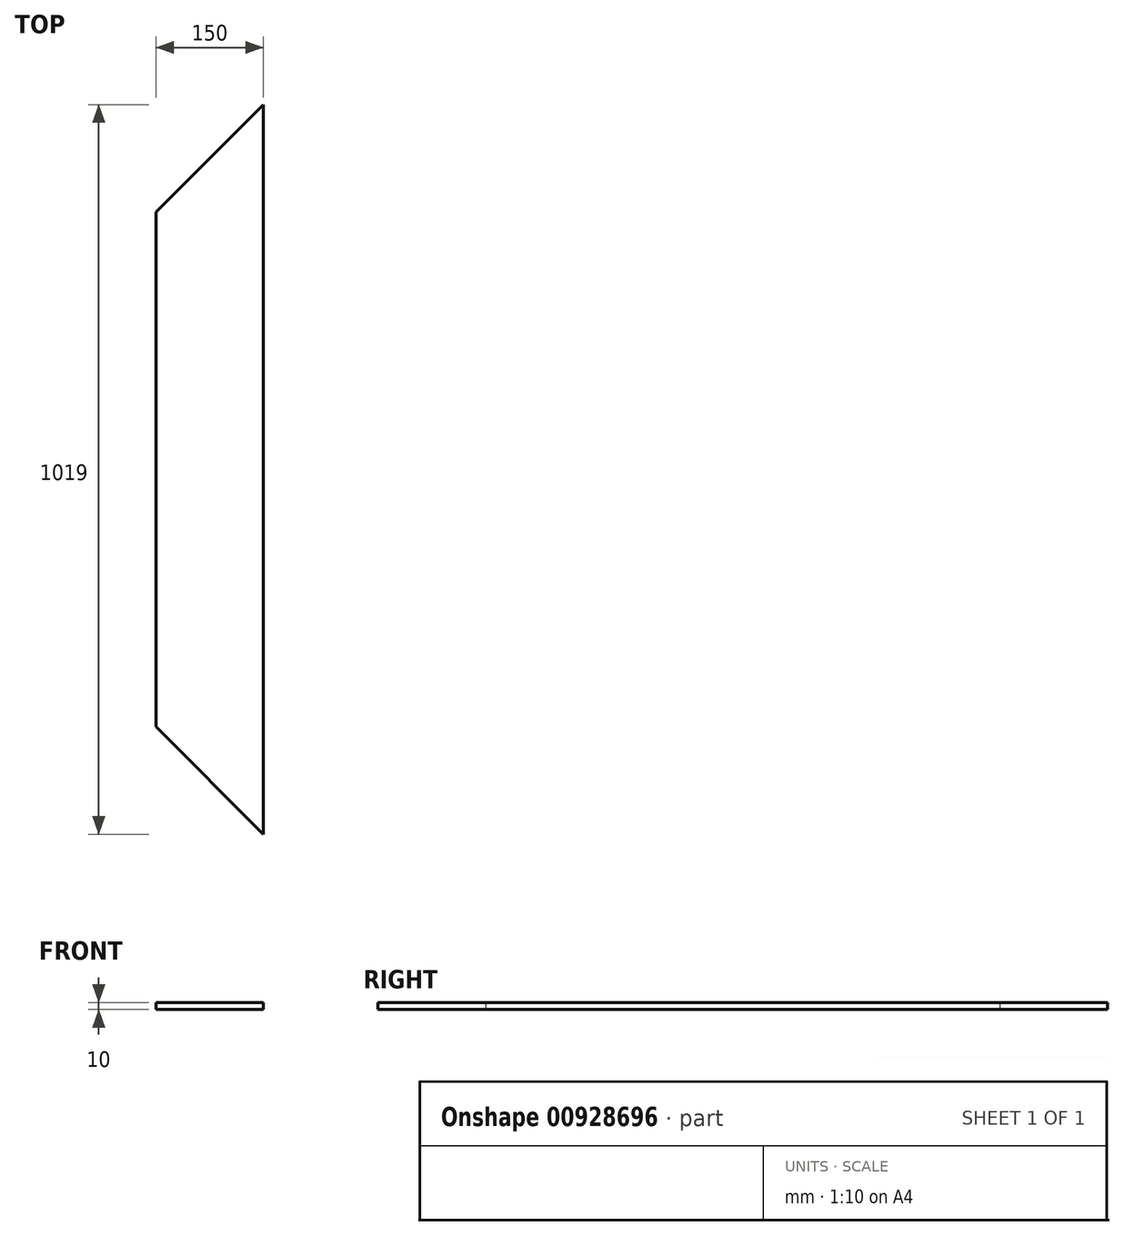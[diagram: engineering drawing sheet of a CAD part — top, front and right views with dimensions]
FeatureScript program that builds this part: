
annotation { "Feature Type Name" : "Feature", "Feature Type Description" : "" }
export const myFeature = defineFeature(function(context is Context, id is Id, definition is map)
    precondition{}
    {
        {
            var Q0;
            Q0=qCreatedBy(makeId("Front.planeOp"),FACE);
            var sketch = newSketch(context, id + "F0", { "sketchPlane" : qUnion([Q0])});
            skLineSegment(sketch, "E0.bottom", {"start": v(-74.52, -26.74) * mm, "end": v(75.48, -26.74) * mm});
            skLineSegment(sketch, "E0.top", {"start": v(-74.52, -36.74) * mm, "end": v(75.48, -36.74) * mm});
            skLineSegment(sketch, "E0.left", {"start": v(-74.52, -26.74) * mm, "end": v(-74.52, -36.74) * mm});
            skLineSegment(sketch, "E0.right", {"start": v(75.48, -26.74) * mm, "end": v(75.48, -36.74) * mm});
            skSolve(sketch);
        }
        {
            var Q0;
            Q0 = qSketchRegion(id + "F0", true);
            extrude(context, id + "F1", {"entities" : qUnion([Q0]), "depth" : 1019 * mm, "offsetDistance" : 25 * mm});
        }
        {
            var Q0;
            Q0=makeQuery(id+"F1.opExtrude","SWEPT_FACE",FACE,{"disambiguationData":[OSD([sQuery(id+"F0.wireOp",EDGE,"E0.bottom")])]});
            var sketch = newSketch(context, id + "F2", { "sketchPlane" : qUnion([Q0])});
            skLineSegment(sketch, "E1", {"start": v(75.48, 0) * mm, "end": v(-74.52, -150) * mm});
            skLineSegment(sketch, "E2", {"start": v(-74.52, -150) * mm, "end": v(-107.99, -156.75) * mm});
            skLineSegment(sketch, "E3", {"start": v(-164.14, -150) * mm, "end": v(-164.14, 159.84) * mm});
            skLineSegment(sketch, "E4", {"start": v(-164.14, 159.84) * mm, "end": v(178, 169.1) * mm});
            skLineSegment(sketch, "E5", {"start": v(178, 169.1) * mm, "end": v(75.48, 0) * mm});
            skLineSegment(sketch, "E6", {"start": v(-107.99, -156.75) * mm, "end": v(-164.14, -150) * mm});
            skSolve(sketch);
        }
        {
            var Q0;
            Q0 = qSketchRegion(id + "F2", true);
            var Q1;
            Q1=sQuery(id+"F2.wireOp",EDGE,"E1");
            extrude(context, id + "F3", {"entities" : qUnion([Q0]), "operationType" : NewBodyOperationType.REMOVE, "surfaceEntities" : qUnion([Q1]), "endBound" : BoundingType.THROUGH_ALL, "oppositeDirection" : true, "depth" : 25 * mm, "offsetDistance" : 25 * mm, "hasSecondDirection" : true, "secondDirectionBound" : SecondDirectionBoundingType.THROUGH_ALL, "secondDirectionOppositeDirection" : false, "secondDirectionDepth" : 25 * mm});
        }
        {
            var Q0;
            Q0=makeQuery(id+"F1.opExtrude","SWEPT_FACE",FACE,{"disambiguationData":[OSD([sQuery(id+"F0.wireOp",EDGE,"E0.bottom")])]});
            var sketch = newSketch(context, id + "F4", { "sketchPlane" : qUnion([Q0])});
            skLineSegment(sketch, "E7", {"start": v(75.48, -1019) * mm, "end": v(-74.52, -869) * mm});
            skLineSegment(sketch, "E8", {"start": v(-74.52, -869) * mm, "end": v(-237.24, -869) * mm});
            skLineSegment(sketch, "E9", {"start": v(-237.24, -869) * mm, "end": v(-237.24, -1200.16) * mm});
            skLineSegment(sketch, "E10", {"start": v(-237.24, -1200.16) * mm, "end": v(72.76, -1200.16) * mm});
            skLineSegment(sketch, "E11", {"start": v(72.76, -1200.16) * mm, "end": v(75.48, -1019) * mm});
            skSolve(sketch);
        }
        {
            var Q0;
            Q0 = qSketchRegion(id + "F4", true);
            extrude(context, id + "F5", {"entities" : qUnion([Q0]), "operationType" : NewBodyOperationType.REMOVE, "endBound" : BoundingType.THROUGH_ALL, "depth" : 25 * mm, "offsetDistance" : 25 * mm, "hasSecondDirection" : true, "secondDirectionBound" : SecondDirectionBoundingType.THROUGH_ALL, "secondDirectionOppositeDirection" : true, "secondDirectionDepth" : 25 * mm});
        }
    });
